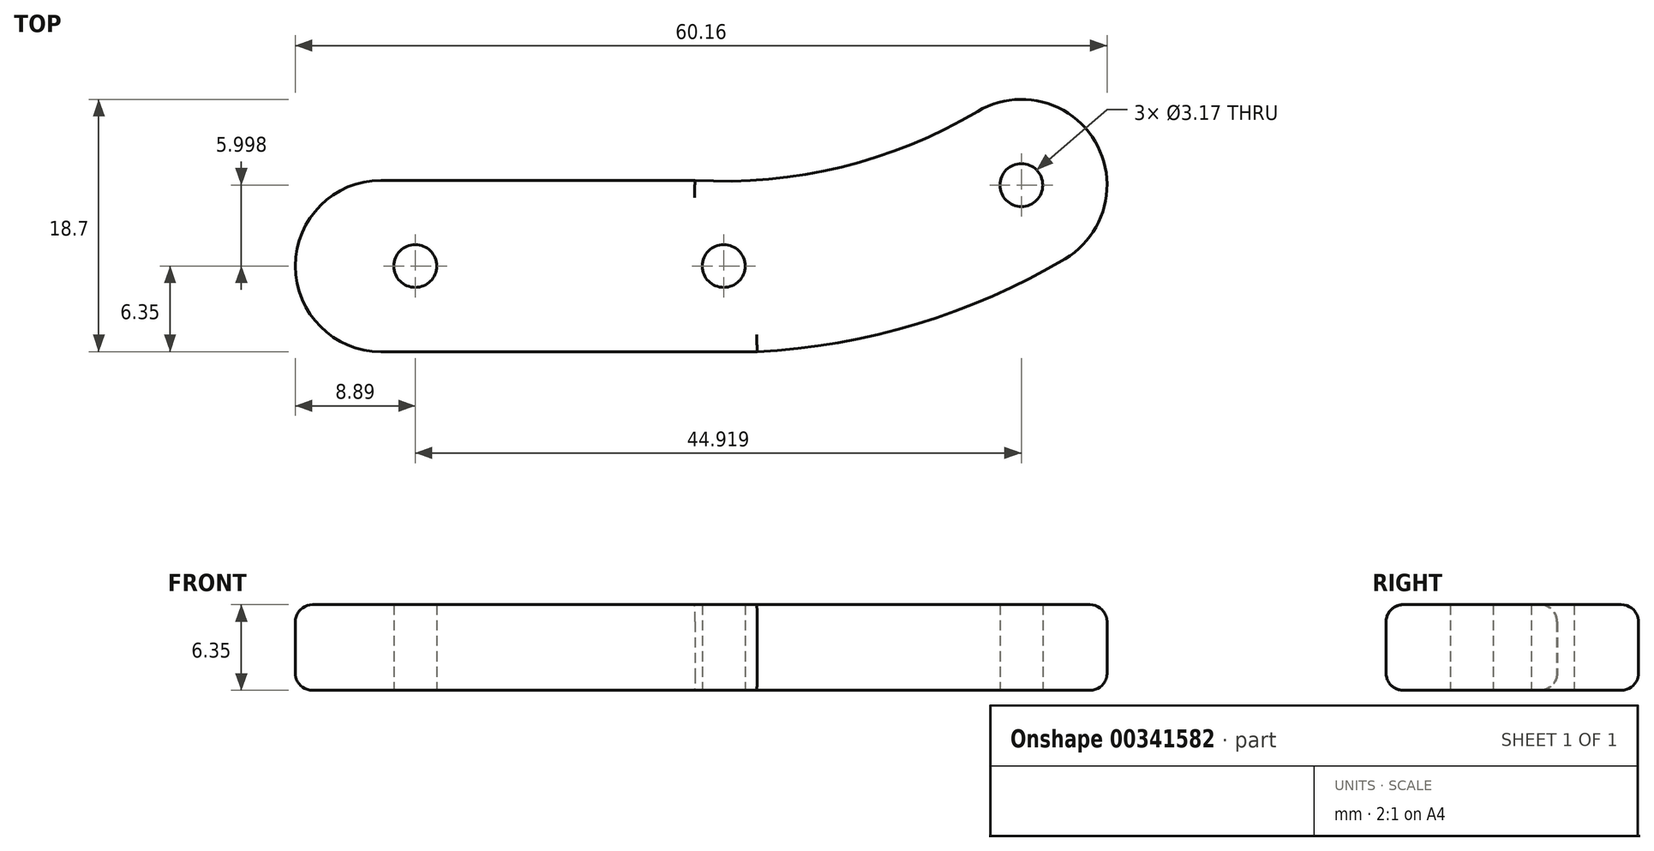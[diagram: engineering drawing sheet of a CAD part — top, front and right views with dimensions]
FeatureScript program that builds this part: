
annotation { "Feature Type Name" : "Feature", "Feature Type Description" : "" }
export const myFeature = defineFeature(function(context is Context, id is Id, definition is map)
    precondition{}
    {
        {
            var Q0;
            Q0=qCreatedBy(makeId("Top.planeOp"),FACE);
            var sketch = newSketch(context, id + "F0", { "sketchPlane" : qUnion([Q0])});
            skLineSegment(sketch, "E0.bottom", {"start": v(2.47, -6.35) * mm, "end": v(-25.4, -6.35) * mm});
            skLineSegment(sketch, "E0.top", {"start": v(-2.13, 6.35) * mm, "end": v(-25.4, 6.35) * mm});
            skLineSegment(sketch, "E0.left", {"start": v(31.75, 0) * mm, "end": v(31.75, 0) * mm});
            skLineSegment(sketch, "E0.right", {"start": v(-31.75, 0) * mm, "end": v(-31.75, 0) * mm});
            skPoint(sketch, "E0.middle", {"position": v(0, 0) * mm});
            skCircle(sketch, "E1", {"center": v(-22.86, 0) * mm, "radius": 1.59 * mm});
            skCircle(sketch, "E2", {"center": v(0, 0) * mm, "radius": 1.59 * mm});
            skPoint(sketch, "E3.visualSharp", {"position": v(-31.75, 6.35) * mm});
            skArc(sketch, "E3.filletArc", {"start": v(-25.4, 6.35) * mm, "mid": v(-29.9, 4.5) * mm, "end": v(-31.75, 0) * mm});
            skPoint(sketch, "E4.visualSharp", {"position": v(-31.75, -6.35) * mm});
            skArc(sketch, "E4.filletArc", {"start": v(-31.75, 0) * mm, "mid": v(-29.9, -4.5) * mm, "end": v(-25.4, -6.35) * mm});
            skPoint(sketch, "E5.visualSharp", {"position": v(31.75, 6.35) * mm});
            skPoint(sketch, "E6.visualSharp", {"position": v(31.75, -6.35) * mm});
            skArc(sketch, "E7", {"start": v(-2.13, 6.35) * mm, "mid": v(8.72, 7.34) * mm, "end": v(18.82, 11.46) * mm});
            skArc(sketch, "E8.0", {"start": v(2.47, -6.35) * mm, "mid": v(14.3, -4.3) * mm, "end": v(25.3, 0.54) * mm});
            skLineSegment(sketch, "E9", {"start": v(26.98, 10) * mm, "end": v(26.98, 10) * mm});
            skPoint(sketch, "E10.visualSharp", {"position": v(23.27, 14.57) * mm});
            skArc(sketch, "E10.filletArc", {"start": v(26.98, 10) * mm, "mid": v(23.17, 12.25) * mm, "end": v(18.82, 11.46) * mm});
            skPoint(sketch, "E11.visualSharp", {"position": v(31.29, 4.72) * mm});
            skArc(sketch, "E11.filletArc", {"start": v(25.3, 0.54) * mm, "mid": v(28.31, 4.89) * mm, "end": v(26.98, 10) * mm});
            skPoint(sketch, "E5.filletArc.end.orphan", {"position": v(21.13, 6.35) * mm});
            skCircle(sketch, "E12", {"center": v(22.06, 6) * mm, "radius": 1.59 * mm});
            skSolve(sketch);
        }
        {
            var Q0;
            Q0 = qSketchRegion(id + "F0", true);
            extrude(context, id + "F1", {"entities" : qUnion([Q0]), "depth" : 6.35 * mm});
        }
        {
            var Q0;
            Q0=makeQuery(id+"F1.opExtrude","CAP_EDGE",EDGE,{"disambiguationData":[OSD([sQuery(id+"F0.wireOp",EDGE,"E10.filletArc"),sQuery(id+"F0.wireOp",EDGE,"E11.filletArc")])],"isStart":true});
            var Q1;
            Q1=makeQuery(id+"F1.opExtrude","CAP_EDGE",EDGE,{"disambiguationData":[OSD([sQuery(id+"F0.wireOp",EDGE,"E7")])],"isStart":true});
            var Q2;
            Q2=makeQuery(id+"F1.opExtrude","CAP_EDGE",EDGE,{"disambiguationData":[OSD([sQuery(id+"F0.wireOp",EDGE,"E0.top")])],"isStart":true});
            var Q3;
            Q3=makeQuery(id+"F1.opExtrude","CAP_EDGE",EDGE,{"disambiguationData":[OSD([sQuery(id+"F0.wireOp",EDGE,"E10.filletArc"),sQuery(id+"F0.wireOp",EDGE,"E11.filletArc")])],"isStart":false});
            var Q4;
            Q4=makeQuery(id+"F1.opExtrude","CAP_EDGE",EDGE,{"disambiguationData":[OSD([sQuery(id+"F0.wireOp",EDGE,"E7")])],"isStart":false});
            var Q5;
            Q5=makeQuery(id+"F1.opExtrude","CAP_EDGE",EDGE,{"disambiguationData":[OSD([sQuery(id+"F0.wireOp",EDGE,"E0.top")])],"isStart":false});
            fillet(context, id + "F2", {"entities" : qUnion([Q0, Q1, Q2, Q3, Q4, Q5]), "radius" : 1.27 * mm, "tangentPropagation" : true, "allowEdgeOverflow" : false});
        }
    });
